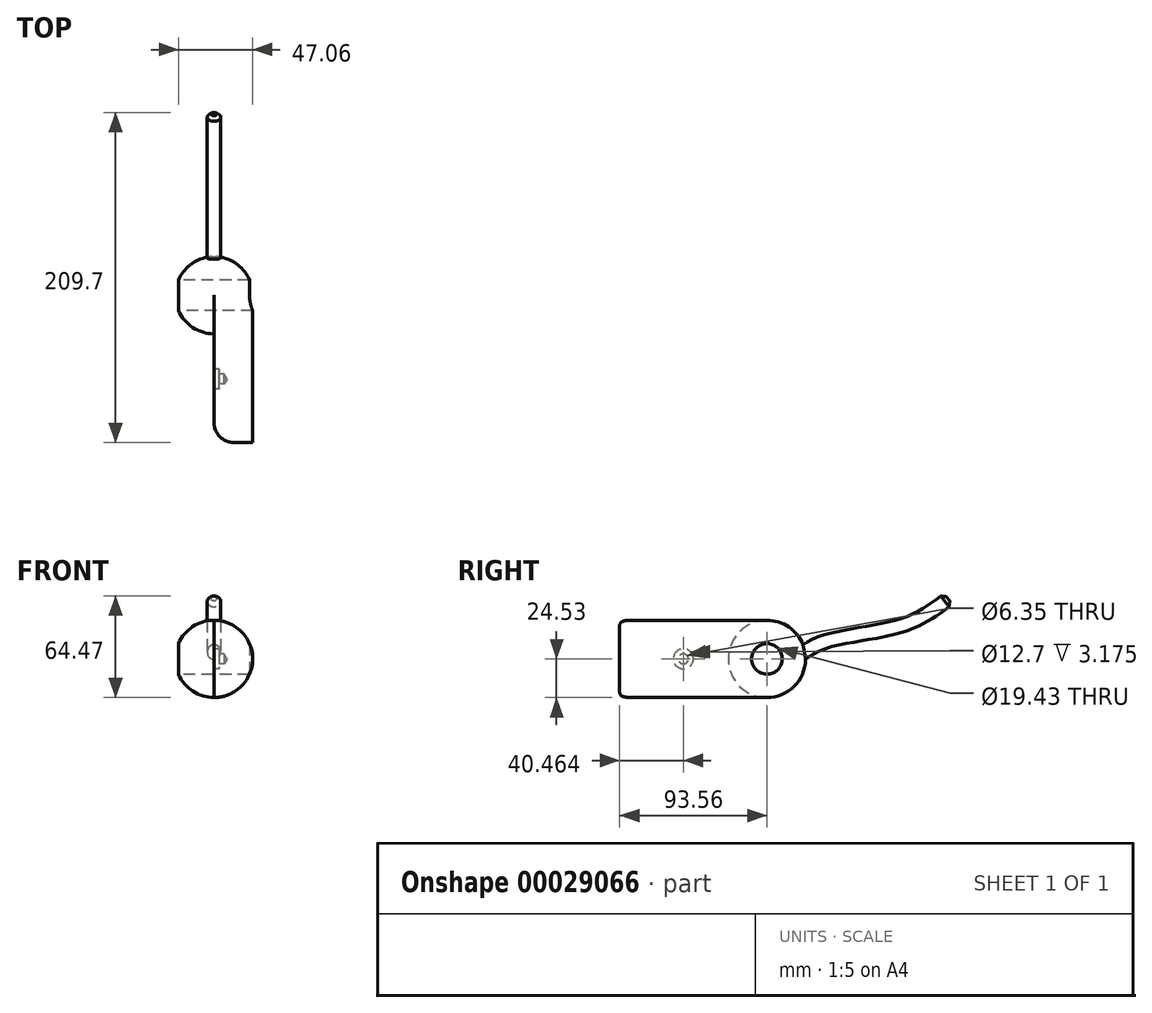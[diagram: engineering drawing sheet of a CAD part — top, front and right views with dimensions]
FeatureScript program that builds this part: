
annotation { "Feature Type Name" : "Feature", "Feature Type Description" : "" }
export const myFeature = defineFeature(function(context is Context, id is Id, definition is map)
    precondition{}
    {
        {
            var Q0;
            Q0=qCreatedBy(makeId("Front.planeOp"),FACE);
            var sketch = newSketch(context, id + "F0", { "sketchPlane" : qUnion([Q0])});
            skArc(sketch, "E0", {"start": v(0, -24.53) * mm, "mid": v(24.53, 0) * mm, "end": v(0, 24.53) * mm});
            skLineSegment(sketch, "E1", {"start": v(0, 24.53) * mm, "end": v(0, -24.53) * mm});
            skSolve(sketch);
        }
        {
            var Q0;
            Q0=makeQuery(id+"F0.imprint","IMPRINT",FACE,{"disambiguationData":[TD([[makeQuery(id+"F0.imprint","IMPRINT",EDGE,{"derivedFrom":sQuery(id+"F0.wireOp",EDGE,"E0")}),1.0]])]});
            var Q1;
            Q1=sQuery(id+"F0.wireOp",EDGE,"E1");
            revolve(context, id + "F1", {"entities" : qUnion([Q0]), "axis" : qUnion([Q1]), "revolveType" : RevolveType.FULL});
        }
        {
            var Q0;
            Q0=makeQuery(id+"F0.imprint","IMPRINT",FACE,{"disambiguationData":[TD([[makeQuery(id+"F0.imprint","IMPRINT",EDGE,{"derivedFrom":sQuery(id+"F0.wireOp",EDGE,"E0")}),1.0]])]});
            extrude(context, id + "F2", {"entities" : qUnion([Q0]), "operationType" : NewBodyOperationType.ADD, "depth" : 93.56 * mm});
        }
        {
            var Q0;
            Q0=makeQuery(id+"F2.opExtrude","CAP_EDGE",EDGE,{"disambiguationData":[OSD([sQuery(id+"F0.wireOp",EDGE,"E1")])],"isStart":false});
            fillet(context, id + "F3", {"entities" : qUnion([Q0]), "radius" : 12.7 * mm, "tangentPropagation" : true, "allowEdgeOverflow" : false});
        }
        {
            var Q0;
            Q0=makeQuery(id+"F2.opExtrude","SWEPT_FACE",FACE,{"disambiguationData":[OSD([sQuery(id+"F0.wireOp",EDGE,"E1")])]});
            var sketch = newSketch(context, id + "F4", { "sketchPlane" : qUnion([Q0])});
            skPoint(sketch, "E2", {"position": v(53.1, 0) * mm});
            skSolve(sketch);
        }
        {
            var Q0;
            Q0=sQuery(id+"F4.wireOp",VERTEX,"E2");
            var Q1;
            Q1=makeQuery(id+"F1.opRevolve","SWEPT_BODY",BODY,{"disambiguationData":[OSD([sQuery(id+"F0.wireOp",EDGE,"E0"),sQuery(id+"F0.wireOp",EDGE,"E1")])]});
            hole(context, id + "F5", {"style" : HoleStyle.C_BORE, "holeDiameter" : 6.35 * mm, "cBoreDiameter" : 12.7 * mm, "cBoreDepth" : 3.17 * mm, "endStyle" : HoleEndStyle.BLIND, "holeDepth" : 6.35 * mm, "locations" : qUnion([Q0]), "scope" : qUnion([Q1])});
        }
        {
            var Q0;
            Q0=qCreatedBy(makeId("Right.planeOp"),FACE);
            var sketch = newSketch(context, id + "F6", { "sketchPlane" : qUnion([Q0])});
            skCircle(sketch, "E3", {"center": v(0, 0) * mm, "radius": 9.71 * mm});
            skSolve(sketch);
        }
        {
            var Q0;
            Q0=makeQuery(id+"F6.imprint","IMPRINT",FACE,{"disambiguationData":[TD([[makeQuery(id+"F6.imprint","IMPRINT",EDGE,{"derivedFrom":sQuery(id+"F6.wireOp",EDGE,"E3")}),1.0]])]});
            var Q1;
            Q1=sQuery(id+"F6.wireOp",EDGE,"E3");
            extrude(context, id + "F7", {"entities" : qUnion([Q0]), "operationType" : NewBodyOperationType.REMOVE, "surfaceEntities" : qUnion([Q1]), "endBound" : BoundingType.SYMMETRIC, "depth" : 74.87 * mm});
        }
        {
            var Q0;
            Q0=qCreatedBy(makeId("Right.planeOp"),FACE);
            var sketch = newSketch(context, id + "F8", { "sketchPlane" : qUnion([Q0])});
            skFitSpline(sketch, "E4", {"points": [v(18.48, 0) * mm, v(36.69, 10.91) * mm, v(85.85, 21.35) * mm, v(115.09, 38.06) * mm], "startDerivative": vector(51.3, 47.39) * mm, "endDerivative": vector(75.18, 57.24) * mm});
            skSolve(sketch);
        }
        {
            var Q0;
            Q0=sQuery(id+"F8.wireOp",VERTEX,"E4.3.internal");
            var Q1;
            Q1=sQuery(id+"F8.wireOp",EDGE,"E4");
            cPlane(context, id + "F9", {"entities" : qUnion([Q0, Q1]), "cplaneType" : CPlaneType.CURVE_POINT, "offset" : 152.4 * mm, "width" : 152.4 * mm, "height" : 152.4 * mm});
        }
        {
            var Q0;
            Q0=qCreatedBy(id+"F9.planeOp",FACE);
            var sketch = newSketch(context, id + "F10", { "sketchPlane" : qUnion([Q0])});
            skCircle(sketch, "E5", {"center": v(0, -39.44) * mm, "radius": 4.28 * mm});
            skSolve(sketch);
        }
        {
            var Q0;
            Q0=makeQuery(id+"F10.imprint","IMPRINT",FACE,{"disambiguationData":[TD([[makeQuery(id+"F10.imprint","IMPRINT",EDGE,{"derivedFrom":sQuery(id+"F10.wireOp",EDGE,"E5")}),1.0]])]});
            var Q1;
            Q1=sQuery(id+"F8.wireOp",EDGE,"E4");
            sweep(context, id + "F11", {"operationType" : NewBodyOperationType.ADD, "profiles" : qUnion([Q0]), "path" : qUnion([Q1])});
        }
        {
            var Q0;
            Q0=makeQuery(id+"F11.opSweep","CAP_EDGE",EDGE,{"disambiguationData":[OSD([sQuery(id+"F8.wireOp",VERTEX,"E4.end"),sQuery(id+"F10.wireOp",EDGE,"E5")])],"isStart":true});
            chamfer(context, id + "F12", {"entities" : qUnion([Q0]), "width" : 2.54 * mm, "tangentPropagation" : true});
        }
    });
